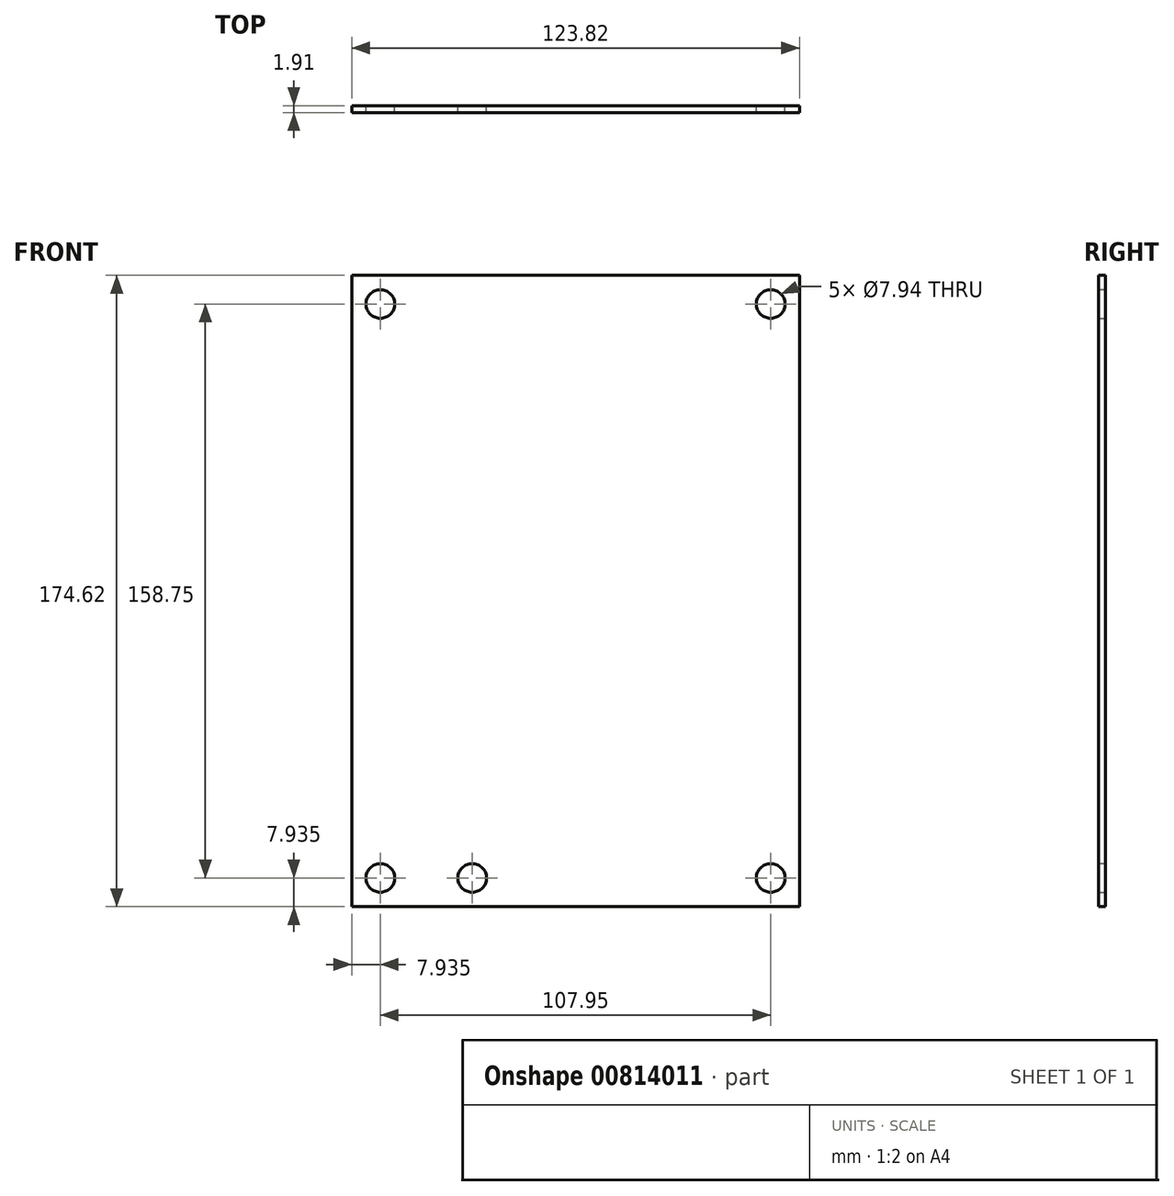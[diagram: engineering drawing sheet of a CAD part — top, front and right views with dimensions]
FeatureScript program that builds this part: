
annotation { "Feature Type Name" : "Feature", "Feature Type Description" : "" }
export const myFeature = defineFeature(function(context is Context, id is Id, definition is map)
    precondition{}
    {
        {
            var Q0;
            Q0=qCreatedBy(makeId("Front.planeOp"),FACE);
            var sketch = newSketch(context, id + "F0", { "sketchPlane" : qUnion([Q0])});
            skLineSegment(sketch, "E0.bottom", {"start": v(61.91, 87.31) * mm, "end": v(-61.91, 87.31) * mm});
            skLineSegment(sketch, "E0.top", {"start": v(61.91, -87.31) * mm, "end": v(-61.91, -87.31) * mm});
            skLineSegment(sketch, "E0.left", {"start": v(61.91, 87.31) * mm, "end": v(61.91, -87.31) * mm});
            skLineSegment(sketch, "E0.right", {"start": v(-61.91, 87.31) * mm, "end": v(-61.91, -87.31) * mm});
            skPoint(sketch, "E0.middle", {"position": v(0, 0) * mm});
            skCircle(sketch, "E1", {"center": v(-53.97, 79.38) * mm, "radius": 3.97 * mm});
            skCircle(sketch, "E2", {"center": v(53.98, 79.38) * mm, "radius": 3.97 * mm});
            skCircle(sketch, "E3", {"center": v(-53.98, -79.38) * mm, "radius": 3.97 * mm});
            skCircle(sketch, "E4", {"center": v(53.97, -79.38) * mm, "radius": 3.97 * mm});
            skCircle(sketch, "E5", {"center": v(-28.58, -79.38) * mm, "radius": 3.97 * mm});
            skSolve(sketch);
        }
        {
            var Q0;
            Q0=qSketchRegion(id+"F0",true);
            extrude(context, id + "F1", {"entities" : qUnion([Q0]), "depth" : 1.9 * mm, "offsetDistance" : 25.4 * mm});
        }
    });
